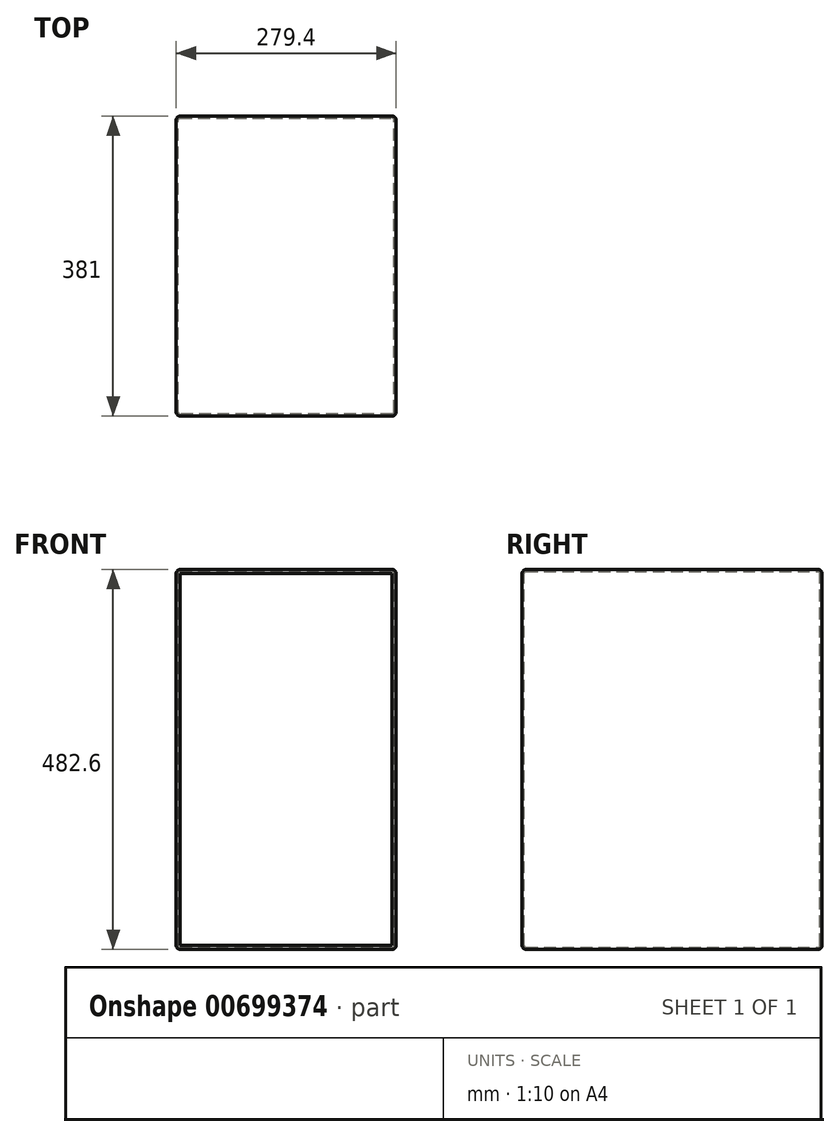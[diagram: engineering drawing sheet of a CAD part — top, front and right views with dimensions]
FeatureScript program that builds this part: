
annotation { "Feature Type Name" : "Feature", "Feature Type Description" : "" }
export const myFeature = defineFeature(function(context is Context, id is Id, definition is map)
    precondition{}
    {
        {
            var Q0;
            Q0=qCreatedBy(makeId("Front.planeOp"),FACE);
            var sketch = newSketch(context, id + "F0", { "sketchPlane" : qUnion([Q0])});
            skLineSegment(sketch, "E0.bottom", {"start": v(-139.7, -241.3) * mm, "end": v(139.7, -241.3) * mm});
            skLineSegment(sketch, "E0.top", {"start": v(-139.7, 241.3) * mm, "end": v(139.7, 241.3) * mm});
            skLineSegment(sketch, "E0.left", {"start": v(-139.7, -241.3) * mm, "end": v(-139.7, 241.3) * mm});
            skLineSegment(sketch, "E0.right", {"start": v(139.7, -241.3) * mm, "end": v(139.7, 241.3) * mm});
            skPoint(sketch, "E0.middle", {"position": v(0, 0) * mm});
            skSolve(sketch);
        }
        {
            var Q0;
            Q0 = qSketchRegion(id + "F0", true);
            extrude(context, id + "F1", {"entities" : qUnion([Q0]), "depth" : 381 * mm, "offsetDistance" : 25.4 * mm});
        }
        {
            var Q0;
            Q0=makeQuery(id+"F1.opExtrude","CAP_FACE",FACE,{"disambiguationData":[OSD([sQuery(id+"F0.wireOp",EDGE,"E0.bottom"),sQuery(id+"F0.wireOp",EDGE,"E0.top"),sQuery(id+"F0.wireOp",EDGE,"E0.left"),sQuery(id+"F0.wireOp",EDGE,"E0.right")])],"isStart":false});
            fillet(context, id + "F2", {"entities" : qUnion([Q0]), "radius" : 5.08 * mm, "tangentPropagation" : true, "allowEdgeOverflow" : false});
        }
        {
            var Q0;
            Q0=makeQuery(id+"F1.opExtrude","SWEPT_FACE",FACE,{"disambiguationData":[OSD([sQuery(id+"F0.wireOp",EDGE,"E0.left")])]});
            fillet(context, id + "F3", {"entities" : qUnion([Q0]), "radius" : 5.08 * mm, "tangentPropagation" : true, "allowEdgeOverflow" : false});
        }
        {
            var Q0;
            Q0=makeQuery(id+"F1.opExtrude","CAP_FACE",FACE,{"disambiguationData":[OSD([sQuery(id+"F0.wireOp",EDGE,"E0.bottom"),sQuery(id+"F0.wireOp",EDGE,"E0.top"),sQuery(id+"F0.wireOp",EDGE,"E0.left"),sQuery(id+"F0.wireOp",EDGE,"E0.right")])],"isStart":true});
            fillet(context, id + "F4", {"entities" : qUnion([Q0]), "radius" : 5.08 * mm, "tangentPropagation" : true, "allowEdgeOverflow" : false});
        }
        {
            var Q0;
            Q0=makeQuery(id+"F1.opExtrude","SWEPT_FACE",FACE,{"disambiguationData":[OSD([sQuery(id+"F0.wireOp",EDGE,"E0.right")])]});
            fillet(context, id + "F5", {"entities" : qUnion([Q0]), "radius" : 5.08 * mm, "tangentPropagation" : true, "allowEdgeOverflow" : false});
        }
        {
            var Q0;
            Q0=makeQuery(id+"F1.opExtrude","CAP_FACE",FACE,{"disambiguationData":[OSD([sQuery(id+"F0.wireOp",EDGE,"E0.bottom"),sQuery(id+"F0.wireOp",EDGE,"E0.top"),sQuery(id+"F0.wireOp",EDGE,"E0.left"),sQuery(id+"F0.wireOp",EDGE,"E0.right")])],"isStart":false});
            shell(context, id + "F6", {"entities" : qUnion([Q0]), "thickness" : 2.54 * mm});
        }
    });
